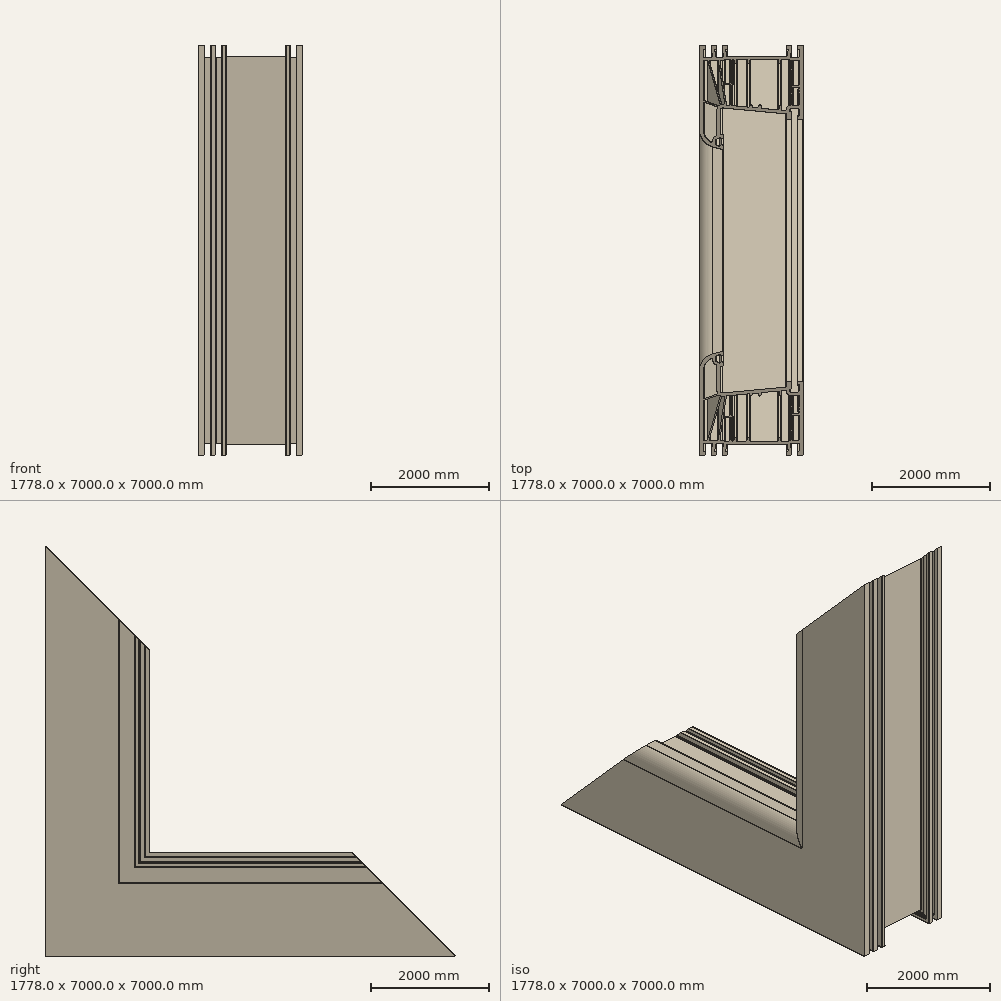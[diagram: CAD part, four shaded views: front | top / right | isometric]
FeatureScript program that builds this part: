
annotation { "Feature Type Name" : "Feature", "Feature Type Description" : "" }
export const myFeature = defineFeature(function(context is Context, id is Id, definition is map)
    precondition{}
    {
        {
            var Q0;
            Q0=qCreatedBy(makeId("Front.planeOp"),FACE);
            var sketch = newSketch(context, id + "F0", { "sketchPlane" : qUnion([Q0])});
            skLineSegment(sketch, "E0", {"start": v(-889, -889) * mm, "end": v(-787.4, -889) * mm});
            skLineSegment(sketch, "E1", {"start": v(-508, 723.9) * mm, "end": v(-520.7, 723.9) * mm});
            skLineSegment(sketch, "E2", {"start": v(-520.7, 723.9) * mm, "end": v(-520.7, 701.04) * mm});
            skLineSegment(sketch, "E3", {"start": v(787.4, -889) * mm, "end": v(889, -889) * mm});
            skLineSegment(sketch, "E4", {"start": v(889, -889) * mm, "end": v(889, 355.6) * mm});
            skLineSegment(sketch, "E5", {"start": v(863.6, 381) * mm, "end": v(787.4, 381) * mm});
            skLineSegment(sketch, "E6", {"start": v(787.4, 381) * mm, "end": v(787.4, 314.96) * mm});
            skLineSegment(sketch, "E7", {"start": v(673.1, 241.3) * mm, "end": v(685.8, 241.3) * mm});
            skLineSegment(sketch, "E8", {"start": v(685.8, 241.3) * mm, "end": v(685.8, 381) * mm});
            skLineSegment(sketch, "E9", {"start": v(685.8, 381) * mm, "end": v(596.9, 381) * mm});
            skLineSegment(sketch, "E10", {"start": v(-889, 548.53) * mm, "end": v(-889, -889) * mm});
            skLineSegment(sketch, "E11", {"start": v(-482.6, 698.5) * mm, "end": v(-508, 723.9) * mm});
            skLineSegment(sketch, "E12", {"start": v(-482.6, 647.7) * mm, "end": v(-482.6, 698.5) * mm});
            skLineSegment(sketch, "E13", {"start": v(-520.7, 635) * mm, "end": v(-495.3, 635) * mm});
            skLineSegment(sketch, "E14", {"start": v(-589.28, 648.94) * mm, "end": v(-589.28, 635) * mm});
            skLineSegment(sketch, "E15", {"start": v(-623.74, 673.1) * mm, "end": v(-596.61, 660.45) * mm});
            skLineSegment(sketch, "E16", {"start": v(-660.4, 753.62) * mm, "end": v(-660.4, 730.65) * mm});
            skLineSegment(sketch, "E17", {"start": v(-820.42, 91.47) * mm, "end": v(-820.42, 548.53) * mm});
            skLineSegment(sketch, "E18", {"start": v(-812.06, 49.34) * mm, "end": v(-561.15, 140.67) * mm});
            skLineSegment(sketch, "E19", {"start": v(-820.42, -617.22) * mm, "end": v(-820.42, 37.41) * mm});
            skLineSegment(sketch, "E20", {"start": v(-587.31, 158.18) * mm, "end": v(-803.38, 79.54) * mm});
            skLineSegment(sketch, "E21", {"start": v(820.42, -215.9) * mm, "end": v(820.42, -617.22) * mm});
            skLineSegment(sketch, "E22", {"start": v(718.82, -203.2) * mm, "end": v(807.72, -203.2) * mm});
            skLineSegment(sketch, "E23", {"start": v(706.12, -617.22) * mm, "end": v(706.12, -215.9) * mm});
            skLineSegment(sketch, "E24", {"start": v(680.72, -495.3) * mm, "end": v(680.72, -618.92) * mm});
            skLineSegment(sketch, "E25", {"start": v(665.48, -482.6) * mm, "end": v(668.02, -482.6) * mm});
            skLineSegment(sketch, "E26", {"start": v(665.48, -457.2) * mm, "end": v(665.48, -482.6) * mm});
            skLineSegment(sketch, "E27", {"start": v(668.02, -457.2) * mm, "end": v(665.48, -457.2) * mm});
            skLineSegment(sketch, "E28", {"start": v(680.72, -88.9) * mm, "end": v(680.72, -444.5) * mm});
            skLineSegment(sketch, "E29", {"start": v(665.48, -76.2) * mm, "end": v(668.02, -76.2) * mm});
            skLineSegment(sketch, "E30", {"start": v(665.48, -50.8) * mm, "end": v(665.48, -76.2) * mm});
            skLineSegment(sketch, "E31", {"start": v(668.02, -50.8) * mm, "end": v(665.48, -50.8) * mm});
            skLineSegment(sketch, "E32", {"start": v(680.72, 122.06) * mm, "end": v(680.72, -38.1) * mm});
            skLineSegment(sketch, "E33", {"start": v(706.12, -165.1) * mm, "end": v(706.12, 121.92) * mm});
            skLineSegment(sketch, "E34", {"start": v(807.72, -177.8) * mm, "end": v(718.82, -177.8) * mm});
            skLineSegment(sketch, "E35", {"start": v(820.42, -152.4) * mm, "end": v(820.42, -165.1) * mm});
            skLineSegment(sketch, "E36", {"start": v(787.4, -139.7) * mm, "end": v(807.72, -139.7) * mm});
            skLineSegment(sketch, "E37", {"start": v(787.4, -114.3) * mm, "end": v(787.4, -139.7) * mm});
            skLineSegment(sketch, "E38", {"start": v(807.72, -114.3) * mm, "end": v(787.4, -114.3) * mm});
            skLineSegment(sketch, "E39", {"start": v(787.4, -88.9) * mm, "end": v(807.72, -88.9) * mm});
            skLineSegment(sketch, "E40", {"start": v(787.4, -63.5) * mm, "end": v(787.4, -88.9) * mm});
            skLineSegment(sketch, "E41", {"start": v(807.72, -63.5) * mm, "end": v(787.4, -63.5) * mm});
            skLineSegment(sketch, "E42", {"start": v(820.42, 121.92) * mm, "end": v(820.42, -50.8) * mm});
            skLineSegment(sketch, "E43", {"start": v(820.42, 314.96) * mm, "end": v(820.42, 215.9) * mm});
            skLineSegment(sketch, "E44", {"start": v(787.4, 314.96) * mm, "end": v(820.42, 314.96) * mm});
            skLineSegment(sketch, "E45", {"start": v(-520.7, 822.96) * mm, "end": v(-520.7, 800.1) * mm});
            skLineSegment(sketch, "E46", {"start": v(-602.27, 804.86) * mm, "end": v(-538.77, 834.47) * mm});
            skLineSegment(sketch, "E47", {"start": v(-609.6, 730.65) * mm, "end": v(-609.6, 793.35) * mm});
            skLineSegment(sketch, "E48", {"start": v(-538.77, 689.53) * mm, "end": v(-602.27, 719.14) * mm});
            skLineSegment(sketch, "E49", {"start": v(787.4, -822.96) * mm, "end": v(787.4, -889) * mm});
            skLineSegment(sketch, "E50", {"start": v(820.42, -822.96) * mm, "end": v(787.4, -822.96) * mm});
            skLineSegment(sketch, "E51", {"start": v(820.42, -711.2) * mm, "end": v(820.42, -822.96) * mm});
            skLineSegment(sketch, "E52", {"start": v(525.87, 217.04) * mm, "end": v(578.17, 221.93) * mm});
            skLineSegment(sketch, "E53", {"start": v(179.16, 184.6) * mm, "end": v(462.37, 211.1) * mm});
            skLineSegment(sketch, "E54", {"start": v(26.4, 170.31) * mm, "end": v(102.96, 177.48) * mm});
            skLineSegment(sketch, "E55", {"start": v(-323.76, 137.56) * mm, "end": v(-49.4, 163.22) * mm});
            skLineSegment(sketch, "E56", {"start": v(-417.58, 128.78) * mm, "end": v(-374.56, 132.8) * mm});
            skLineSegment(sketch, "E57", {"start": v(-486.55, 122.33) * mm, "end": v(-469.67, 123.9) * mm});
            skLineSegment(sketch, "E58", {"start": v(-589.28, 635) * mm, "end": v(-589.28, 215.9) * mm});
            skLineSegment(sketch, "E59", {"start": v(-533.4, 215.9) * mm, "end": v(-533.4, 622.3) * mm});
            skLineSegment(sketch, "E60", {"start": v(572.97, 277.57) * mm, "end": v(-491.75, 177.97) * mm});
            skLineSegment(sketch, "E61", {"start": v(795.02, 190.5) * mm, "end": v(673.1, 190.5) * mm});
            skLineSegment(sketch, "E62", {"start": v(718.82, 134.62) * mm, "end": v(807.72, 134.62) * mm});
            skLineSegment(sketch, "E63", {"start": v(-360.68, -248.92) * mm, "end": v(-360.68, -629.92) * mm});
            skLineSegment(sketch, "E64", {"start": v(-470.96, -236.22) * mm, "end": v(-373.38, -236.22) * mm});
            skLineSegment(sketch, "E65", {"start": v(-538.56, -615.34) * mm, "end": v(-483.52, -247.04) * mm});
            skLineSegment(sketch, "E66", {"start": v(-455.93, 109.39) * mm, "end": v(-564.8, -619.1) * mm});
            skLineSegment(sketch, "E67", {"start": v(-476.68, -201.32) * mm, "end": v(-428.96, 118.01) * mm});
            skLineSegment(sketch, "E68", {"start": v(-373.38, -215.9) * mm, "end": v(-464.12, -215.9) * mm});
            skLineSegment(sketch, "E69", {"start": v(-360.68, 120.16) * mm, "end": v(-360.68, -203.2) * mm});
            skLineSegment(sketch, "E70", {"start": v(-335.28, -203.2) * mm, "end": v(-335.28, 124.91) * mm});
            skLineSegment(sketch, "E71", {"start": v(-284.48, -215.9) * mm, "end": v(-322.58, -215.9) * mm});
            skLineSegment(sketch, "E72", {"start": v(-284.48, -241.3) * mm, "end": v(-284.48, -215.9) * mm});
            skLineSegment(sketch, "E73", {"start": v(-322.58, -241.3) * mm, "end": v(-284.48, -241.3) * mm});
            skLineSegment(sketch, "E74", {"start": v(-335.28, -629.92) * mm, "end": v(-335.28, -254) * mm});
            skLineSegment(sketch, "E75", {"start": v(167.64, 152.4) * mm, "end": v(167.64, 171.96) * mm});
            skLineSegment(sketch, "E76", {"start": v(116.84, 164.83) * mm, "end": v(116.84, 152.4) * mm});
            skLineSegment(sketch, "E77", {"start": v(593.11, 279.46) * mm, "end": v(572.97, 277.57) * mm});
            skLineSegment(sketch, "E78", {"start": v(604.58, 293.2) * mm, "end": v(596.9, 381) * mm});
            skLineSegment(sketch, "E79", {"start": v(-482.6, 825.5) * mm, "end": v(-482.6, 881.38) * mm});
            skLineSegment(sketch, "E80", {"start": v(-508, 800.1) * mm, "end": v(-482.6, 825.5) * mm});
            skLineSegment(sketch, "E81", {"start": v(-520.7, 800.1) * mm, "end": v(-508, 800.1) * mm});
            skLineSegment(sketch, "E82", {"start": v(-406.4, -876.3) * mm, "end": v(-406.4, -822.96) * mm});
            skLineSegment(sketch, "E83", {"start": v(-406.4, -822.96) * mm, "end": v(-444.5, -822.96) * mm});
            skLineSegment(sketch, "E84", {"start": v(-444.5, -822.96) * mm, "end": v(-444.5, -793.3) * mm});
            skLineSegment(sketch, "E85", {"start": v(-419.1, -749.3) * mm, "end": v(-419.1, -711.2) * mm});
            skLineSegment(sketch, "E86", {"start": v(-495.3, -876.3) * mm, "end": v(-482.6, -889) * mm});
            skLineSegment(sketch, "E87", {"start": v(-660.4, -749.3) * mm, "end": v(-685.8, -749.3) * mm});
            skLineSegment(sketch, "E88", {"start": v(-685.8, -749.3) * mm, "end": v(-685.8, -876.3) * mm});
            skLineSegment(sketch, "E89", {"start": v(-685.8, -876.3) * mm, "end": v(-673.1, -889) * mm});
            skLineSegment(sketch, "E90", {"start": v(-673.1, -889) * mm, "end": v(-596.9, -889) * mm});
            skLineSegment(sketch, "E91", {"start": v(-596.9, -889) * mm, "end": v(-596.9, -822.96) * mm});
            skLineSegment(sketch, "E92", {"start": v(-596.9, -822.96) * mm, "end": v(-635, -822.96) * mm});
            skLineSegment(sketch, "E93", {"start": v(-635, -822.96) * mm, "end": v(-635, -793.3) * mm});
            skLineSegment(sketch, "E94", {"start": v(-609.6, -749.3) * mm, "end": v(-609.6, -711.2) * mm});
            skLineSegment(sketch, "E95", {"start": v(-660.4, -711.2) * mm, "end": v(-660.4, -749.3) * mm});
            skLineSegment(sketch, "E96", {"start": v(596.9, -822.96) * mm, "end": v(596.9, -876.3) * mm});
            skLineSegment(sketch, "E97", {"start": v(635, -822.96) * mm, "end": v(596.9, -822.96) * mm});
            skLineSegment(sketch, "E98", {"start": v(635, -793.3) * mm, "end": v(635, -822.96) * mm});
            skLineSegment(sketch, "E99", {"start": v(609.6, -711.2) * mm, "end": v(609.6, -749.3) * mm});
            skLineSegment(sketch, "E100", {"start": v(-257.8, -629.92) * mm, "end": v(-257.8, -603.25) * mm});
            skLineSegment(sketch, "E101", {"start": v(-295.9, -603.25) * mm, "end": v(-295.9, -629.92) * mm});
            skLineSegment(sketch, "E102", {"start": v(-31.75, -629.92) * mm, "end": v(-31.75, -603.25) * mm});
            skLineSegment(sketch, "E103", {"start": v(-69.85, -603.25) * mm, "end": v(-69.85, -629.92) * mm});
            skLineSegment(sketch, "E104", {"start": v(499.11, -629.92) * mm, "end": v(499.11, -603.25) * mm});
            skLineSegment(sketch, "E105", {"start": v(461.01, -603.25) * mm, "end": v(461.01, -629.92) * mm});
            skLineSegment(sketch, "E106", {"start": v(-495.3, -749.3) * mm, "end": v(-495.3, -876.3) * mm});
            skLineSegment(sketch, "E107", {"start": v(-469.9, -749.3) * mm, "end": v(-495.3, -749.3) * mm});
            skLineSegment(sketch, "E108", {"start": v(-469.9, -711.2) * mm, "end": v(-469.9, -749.3) * mm});
            skLineSegment(sketch, "E109", {"start": v(-482.6, -889) * mm, "end": v(-419.1, -889) * mm});
            skLineSegment(sketch, "E110", {"start": v(-419.1, -889) * mm, "end": v(-406.4, -876.3) * mm});
            skLineSegment(sketch, "E111", {"start": v(-820.42, -822.96) * mm, "end": v(-820.42, -711.2) * mm});
            skLineSegment(sketch, "E112", {"start": v(-787.4, -822.96) * mm, "end": v(-820.42, -822.96) * mm});
            skLineSegment(sketch, "E113", {"start": v(-787.4, -889) * mm, "end": v(-787.4, -822.96) * mm});
            skLineSegment(sketch, "E114", {"start": v(-492.2, 888.74) * mm, "end": v(-663.09, 842.95) * mm});
            skLineSegment(sketch, "E115", {"start": v(476.25, 198.46) * mm, "end": v(476.25, 146.05) * mm});
            skLineSegment(sketch, "E116", {"start": v(514.35, 146.05) * mm, "end": v(514.35, 204.4) * mm});
            skLineSegment(sketch, "E117", {"start": v(-718.23, -613.72) * mm, "end": v(-509.92, 112.75) * mm});
            skLineSegment(sketch, "E118", {"start": v(-534.56, 118.96) * mm, "end": v(-746.66, -620.72) * mm});
            skLineSegment(sketch, "E119", {"start": v(660.4, -749.3) * mm, "end": v(660.4, -711.2) * mm});
            skLineSegment(sketch, "E120", {"start": v(685.8, -749.3) * mm, "end": v(660.4, -749.3) * mm});
            skLineSegment(sketch, "E121", {"start": v(685.8, -876.3) * mm, "end": v(685.8, -749.3) * mm});
            skLineSegment(sketch, "E122", {"start": v(673.1, -889) * mm, "end": v(685.8, -876.3) * mm});
            skLineSegment(sketch, "E123", {"start": v(609.6, -889) * mm, "end": v(673.1, -889) * mm});
            skLineSegment(sketch, "E124", {"start": v(596.9, -876.3) * mm, "end": v(609.6, -889) * mm});
            skLineSegment(sketch, "E125", {"start": v(-758.87, -629.92) * mm, "end": v(-807.72, -629.92) * mm});
            skLineSegment(sketch, "E126", {"start": v(-577.36, -629.92) * mm, "end": v(-706.02, -629.92) * mm});
            skLineSegment(sketch, "E127", {"start": v(-495.3, -629.92) * mm, "end": v(-526, -629.92) * mm});
            skLineSegment(sketch, "E128", {"start": v(-373.38, -642.62) * mm, "end": v(-448.12, -642.62) * mm});
            skLineSegment(sketch, "E129", {"start": v(-308.6, -642.62) * mm, "end": v(-322.58, -642.62) * mm});
            skLineSegment(sketch, "E130", {"start": v(-82.55, -642.62) * mm, "end": v(-245.1, -642.62) * mm});
            skLineSegment(sketch, "E131", {"start": v(448.31, -642.62) * mm, "end": v(-19.05, -642.62) * mm});
            skLineSegment(sketch, "E132", {"start": v(638.62, -642.62) * mm, "end": v(511.81, -642.62) * mm});
            skLineSegment(sketch, "E133", {"start": v(807.72, -629.92) * mm, "end": v(718.82, -629.92) * mm});
            skLineSegment(sketch, "E134", {"start": v(685.8, -685.8) * mm, "end": v(795.02, -685.8) * mm});
            skLineSegment(sketch, "E135", {"start": v(-406.4, -698.5) * mm, "end": v(596.9, -698.5) * mm});
            skLineSegment(sketch, "E136", {"start": v(-584.2, -685.8) * mm, "end": v(-495.3, -685.8) * mm});
            skLineSegment(sketch, "E137", {"start": v(-795.02, -685.8) * mm, "end": v(-685.8, -685.8) * mm});
            skArc(sketch, "E138", {"start": v(-663.09, 842.95) * mm, "mid": v(-826.01, 734.09) * mm, "end": v(-889, 548.53) * mm});
            skArc(sketch, "E139", {"start": v(604.58, 293.2) * mm, "mid": v(601.68, 283.97) * mm, "end": v(593.11, 279.46) * mm});
            skArc(sketch, "E140", {"start": v(647.76, 214.11) * mm, "mid": v(654.52, 233.22) * mm, "end": v(673.1, 241.3) * mm});
            skArc(sketch, "E141", {"start": v(514.35, 204.4) * mm, "mid": v(517.66, 212.95) * mm, "end": v(525.87, 217.04) * mm});
            skArc(sketch, "E142", {"start": v(462.37, 211.1) * mm, "mid": v(472.1, 207.84) * mm, "end": v(476.25, 198.46) * mm});
            skArc(sketch, "E143", {"start": v(476.25, 146.05) * mm, "mid": v(495.3, 127) * mm, "end": v(514.35, 146.05) * mm});
            skArc(sketch, "E144", {"start": v(-49.4, 163.22) * mm, "mid": v(-39.9, 160.17) * mm, "end": v(-35.53, 151.19) * mm});
            skArc(sketch, "E145", {"start": v(15, 155.91) * mm, "mid": v(17.61, 165.55) * mm, "end": v(26.4, 170.31) * mm});
            skArc(sketch, "E146", {"start": v(-35.53, 151.19) * mm, "mid": v(-7.8, 127.11) * mm, "end": v(15, 155.91) * mm});
            skArc(sketch, "E147", {"start": v(-706.02, -629.92) * mm, "mid": v(-716.17, -624.86) * mm, "end": v(-718.23, -613.72) * mm});
            skArc(sketch, "E148", {"start": v(-509.92, 112.75) * mm, "mid": v(-505.24, 119.48) * mm, "end": v(-497.42, 121.94) * mm});
            skArc(sketch, "E149", {"start": v(-540.64, 133.58) * mm, "mid": v(-535.04, 127.33) * mm, "end": v(-534.56, 118.96) * mm});
            skArc(sketch, "E150", {"start": v(-746.66, -620.72) * mm, "mid": v(-751.23, -627.36) * mm, "end": v(-758.87, -629.92) * mm});
            skArc(sketch, "E151", {"start": v(660.4, -711.2) * mm, "mid": v(661.27, -704.63) * mm, "end": v(663.8, -698.5) * mm});
            skArc(sketch, "E152", {"start": v(609.6, -749.3) * mm, "mid": v(616.4, -774.7) * mm, "end": v(635, -793.3) * mm});
            skArc(sketch, "E153", {"start": v(596.9, -698.5) * mm, "mid": v(605.88, -702.22) * mm, "end": v(609.6, -711.2) * mm});
            skArc(sketch, "E154", {"start": v(-807.72, -629.92) * mm, "mid": v(-816.7, -626.2) * mm, "end": v(-820.42, -617.22) * mm});
            skArc(sketch, "E155", {"start": v(-454.5, -640.9) * mm, "mid": v(-474.17, -632.71) * mm, "end": v(-495.3, -629.92) * mm});
            skArc(sketch, "E156", {"start": v(-448.12, -642.62) * mm, "mid": v(-451.42, -642.18) * mm, "end": v(-454.5, -640.9) * mm});
            skArc(sketch, "E157", {"start": v(645, -640.9) * mm, "mid": v(641.92, -642.18) * mm, "end": v(638.62, -642.62) * mm});
            skArc(sketch, "E158", {"start": v(670.42, -631.39) * mm, "mid": v(657.3, -635.08) * mm, "end": v(645, -640.9) * mm});
            skArc(sketch, "E159", {"start": v(820.42, -617.22) * mm, "mid": v(816.7, -626.2) * mm, "end": v(807.72, -629.92) * mm});
            skArc(sketch, "E160", {"start": v(795.02, -685.8) * mm, "mid": v(812.98, -693.24) * mm, "end": v(820.42, -711.2) * mm});
            skArc(sketch, "E161", {"start": v(-495.3, -685.8) * mm, "mid": v(-482.6, -689.2) * mm, "end": v(-473.3, -698.5) * mm});
            skArc(sketch, "E162", {"start": v(-820.42, -711.2) * mm, "mid": v(-812.98, -693.24) * mm, "end": v(-795.02, -685.8) * mm});
            skArc(sketch, "E163", {"start": v(663.8, -698.5) * mm, "mid": v(673.1, -689.2) * mm, "end": v(685.8, -685.8) * mm});
            skArc(sketch, "E164", {"start": v(-69.85, -629.92) * mm, "mid": v(-73.57, -638.9) * mm, "end": v(-82.55, -642.62) * mm});
            skArc(sketch, "E165", {"start": v(-31.75, -603.25) * mm, "mid": v(-50.8, -584.2) * mm, "end": v(-69.85, -603.25) * mm});
            skArc(sketch, "E166", {"start": v(-19.05, -642.62) * mm, "mid": v(-28.03, -638.9) * mm, "end": v(-31.75, -629.92) * mm});
            skArc(sketch, "E167", {"start": v(-245.1, -642.62) * mm, "mid": v(-254.1, -638.9) * mm, "end": v(-257.8, -629.92) * mm});
            skArc(sketch, "E168", {"start": v(-257.8, -603.25) * mm, "mid": v(-276.86, -584.2) * mm, "end": v(-295.9, -603.25) * mm});
            skArc(sketch, "E169", {"start": v(-295.9, -629.92) * mm, "mid": v(-299.63, -638.9) * mm, "end": v(-308.6, -642.62) * mm});
            skArc(sketch, "E170", {"start": v(511.81, -642.62) * mm, "mid": v(502.83, -638.9) * mm, "end": v(499.11, -629.92) * mm});
            skArc(sketch, "E171", {"start": v(499.11, -603.25) * mm, "mid": v(480.06, -584.2) * mm, "end": v(461.01, -603.25) * mm});
            skArc(sketch, "E172", {"start": v(461.01, -629.92) * mm, "mid": v(457.3, -638.9) * mm, "end": v(448.31, -642.62) * mm});
            skArc(sketch, "E173", {"start": v(-473.3, -698.5) * mm, "mid": v(-470.77, -704.63) * mm, "end": v(-469.9, -711.2) * mm});
            skArc(sketch, "E174", {"start": v(-444.5, -793.3) * mm, "mid": v(-425.9, -774.7) * mm, "end": v(-419.1, -749.3) * mm});
            skArc(sketch, "E175", {"start": v(-419.1, -711.2) * mm, "mid": v(-415.38, -702.22) * mm, "end": v(-406.4, -698.5) * mm});
            skArc(sketch, "E176", {"start": v(-685.8, -685.8) * mm, "mid": v(-667.84, -693.24) * mm, "end": v(-660.4, -711.2) * mm});
            skArc(sketch, "E177", {"start": v(-635, -793.3) * mm, "mid": v(-616.4, -774.7) * mm, "end": v(-609.6, -749.3) * mm});
            skArc(sketch, "E178", {"start": v(-609.6, -711.2) * mm, "mid": v(-602.16, -693.24) * mm, "end": v(-584.2, -685.8) * mm});
            skArc(sketch, "E179", {"start": v(-482.6, 881.38) * mm, "mid": v(-485.58, 887.43) * mm, "end": v(-492.2, 888.74) * mm});
            skArc(sketch, "E180", {"start": v(-538.77, 834.47) * mm, "mid": v(-526.58, 833.67) * mm, "end": v(-520.7, 822.96) * mm});
            skArc(sketch, "E181", {"start": v(-609.6, 793.35) * mm, "mid": v(-607.61, 800.17) * mm, "end": v(-602.27, 804.86) * mm});
            skArc(sketch, "E182", {"start": v(-602.27, 719.14) * mm, "mid": v(-607.61, 723.83) * mm, "end": v(-609.6, 730.65) * mm});
            skArc(sketch, "E183", {"start": v(-520.7, 701.04) * mm, "mid": v(-526.58, 690.33) * mm, "end": v(-538.77, 689.53) * mm});
            skArc(sketch, "E184", {"start": v(-495.3, 635) * mm, "mid": v(-486.32, 638.72) * mm, "end": v(-482.6, 647.7) * mm});
            skArc(sketch, "E185", {"start": v(-596.61, 660.45) * mm, "mid": v(-591.27, 655.77) * mm, "end": v(-589.28, 648.94) * mm});
            skArc(sketch, "E186", {"start": v(-660.4, 730.65) * mm, "mid": v(-650.46, 696.53) * mm, "end": v(-623.74, 673.1) * mm});
            skArc(sketch, "E187", {"start": v(-678.15, 765.27) * mm, "mid": v(-666.13, 764.23) * mm, "end": v(-660.4, 753.62) * mm});
            skArc(sketch, "E188", {"start": v(-820.42, 548.53) * mm, "mid": v(-781.68, 678.16) * mm, "end": v(-678.15, 765.27) * mm});
            skArc(sketch, "E189", {"start": v(-561.15, 140.67) * mm, "mid": v(-555.13, 141.32) * mm, "end": v(-549.48, 139.11) * mm});
            skArc(sketch, "E190", {"start": v(-820.42, 37.41) * mm, "mid": v(-818.12, 44.7) * mm, "end": v(-812.06, 49.34) * mm});
            skArc(sketch, "E191", {"start": v(-803.38, 79.54) * mm, "mid": v(-815, 81.07) * mm, "end": v(-820.42, 91.47) * mm});
            skArc(sketch, "E192", {"start": v(-580.18, 175.56) * mm, "mid": v(-579.9, 165.3) * mm, "end": v(-587.31, 158.18) * mm});
            skArc(sketch, "E193", {"start": v(807.72, -203.2) * mm, "mid": v(816.7, -206.92) * mm, "end": v(820.42, -215.9) * mm});
            skArc(sketch, "E194", {"start": v(706.12, -215.9) * mm, "mid": v(709.84, -206.92) * mm, "end": v(718.82, -203.2) * mm});
            skArc(sketch, "E195", {"start": v(718.82, -629.92) * mm, "mid": v(709.84, -626.2) * mm, "end": v(706.12, -617.22) * mm});
            skArc(sketch, "E196", {"start": v(680.72, -618.92) * mm, "mid": v(677.81, -627) * mm, "end": v(670.42, -631.39) * mm});
            skArc(sketch, "E197", {"start": v(668.02, -482.6) * mm, "mid": v(677, -486.32) * mm, "end": v(680.72, -495.3) * mm});
            skArc(sketch, "E198", {"start": v(680.72, -444.5) * mm, "mid": v(677, -453.48) * mm, "end": v(668.02, -457.2) * mm});
            skArc(sketch, "E199", {"start": v(668.02, -76.2) * mm, "mid": v(677, -79.92) * mm, "end": v(680.72, -88.9) * mm});
            skArc(sketch, "E200", {"start": v(680.72, -38.1) * mm, "mid": v(677, -47.08) * mm, "end": v(668.02, -50.8) * mm});
            skArc(sketch, "E201", {"start": v(668.7, 134.74) * mm, "mid": v(677.24, 130.8) * mm, "end": v(680.72, 122.06) * mm});
            skArc(sketch, "E202", {"start": v(706.12, 121.92) * mm, "mid": v(709.84, 130.9) * mm, "end": v(718.82, 134.62) * mm});
            skArc(sketch, "E203", {"start": v(718.82, -177.8) * mm, "mid": v(709.84, -174.08) * mm, "end": v(706.12, -165.1) * mm});
            skArc(sketch, "E204", {"start": v(820.42, -165.1) * mm, "mid": v(816.7, -174.08) * mm, "end": v(807.72, -177.8) * mm});
            skArc(sketch, "E205", {"start": v(807.72, -139.7) * mm, "mid": v(816.7, -143.42) * mm, "end": v(820.42, -152.4) * mm});
            skArc(sketch, "E206", {"start": v(820.42, -101.6) * mm, "mid": v(816.7, -110.58) * mm, "end": v(807.72, -114.3) * mm});
            skArc(sketch, "E207", {"start": v(807.72, -88.9) * mm, "mid": v(816.7, -92.62) * mm, "end": v(820.42, -101.6) * mm});
            skArc(sketch, "E208", {"start": v(820.42, -50.8) * mm, "mid": v(816.7, -59.78) * mm, "end": v(807.72, -63.5) * mm});
            skArc(sketch, "E209", {"start": v(889, 355.6) * mm, "mid": v(881.56, 373.56) * mm, "end": v(863.6, 381) * mm});
            skArc(sketch, "E210", {"start": v(807.72, 134.62) * mm, "mid": v(816.7, 130.9) * mm, "end": v(820.42, 121.92) * mm});
            skArc(sketch, "E211", {"start": v(578.17, 221.93) * mm, "mid": v(587.57, 218.97) * mm, "end": v(592.02, 210.18) * mm});
            skArc(sketch, "E212", {"start": v(-497.42, 121.94) * mm, "mid": v(-491.98, 121.98) * mm, "end": v(-486.55, 122.33) * mm});
            skArc(sketch, "E213", {"start": v(-549.48, 139.11) * mm, "mid": v(-545.14, 136.22) * mm, "end": v(-540.64, 133.58) * mm});
            skArc(sketch, "E214", {"start": v(-589.28, 215.9) * mm, "mid": v(-586.98, 195.23) * mm, "end": v(-580.18, 175.56) * mm});
            skArc(sketch, "E215", {"start": v(-533.4, 622.3) * mm, "mid": v(-529.68, 631.28) * mm, "end": v(-520.7, 635) * mm});
            skArc(sketch, "E216", {"start": v(-491.75, 177.97) * mm, "mid": v(-520.96, 187.73) * mm, "end": v(-533.4, 215.9) * mm});
            skArc(sketch, "E217", {"start": v(673.1, 190.5) * mm, "mid": v(655.78, 197.32) * mm, "end": v(647.76, 214.11) * mm});
            skArc(sketch, "E218", {"start": v(820.42, 215.9) * mm, "mid": v(812.98, 197.94) * mm, "end": v(795.02, 190.5) * mm});
            skArc(sketch, "E219", {"start": v(592.02, 210.18) * mm, "mid": v(616.1, 157.96) * mm, "end": v(668.7, 134.74) * mm});
            skArc(sketch, "E220", {"start": v(-360.68, -629.92) * mm, "mid": v(-364.4, -638.9) * mm, "end": v(-373.38, -642.62) * mm});
            skArc(sketch, "E221", {"start": v(-373.38, -236.22) * mm, "mid": v(-364.4, -239.94) * mm, "end": v(-360.68, -248.92) * mm});
            skArc(sketch, "E222", {"start": v(-483.52, -247.04) * mm, "mid": v(-479.25, -239.3) * mm, "end": v(-470.96, -236.22) * mm});
            skArc(sketch, "E223", {"start": v(-526, -629.92) * mm, "mid": v(-535.62, -625.51) * mm, "end": v(-538.56, -615.34) * mm});
            skArc(sketch, "E224", {"start": v(-564.8, -619.1) * mm, "mid": v(-569.07, -626.84) * mm, "end": v(-577.36, -629.92) * mm});
            skArc(sketch, "E225", {"start": v(-469.67, 123.9) * mm, "mid": v(-459.27, 120) * mm, "end": v(-455.93, 109.39) * mm});
            skArc(sketch, "E226", {"start": v(-428.96, 118.01) * mm, "mid": v(-425.13, 125.36) * mm, "end": v(-417.58, 128.78) * mm});
            skArc(sketch, "E227", {"start": v(-464.12, -215.9) * mm, "mid": v(-473.74, -211.5) * mm, "end": v(-476.68, -201.32) * mm});
            skArc(sketch, "E228", {"start": v(-360.68, -203.2) * mm, "mid": v(-364.4, -212.18) * mm, "end": v(-373.38, -215.9) * mm});
            skArc(sketch, "E229", {"start": v(-374.56, 132.8) * mm, "mid": v(-364.83, 129.55) * mm, "end": v(-360.68, 120.16) * mm});
            skArc(sketch, "E230", {"start": v(-335.28, 124.91) * mm, "mid": v(-331.97, 133.46) * mm, "end": v(-323.76, 137.56) * mm});
            skArc(sketch, "E231", {"start": v(-322.58, -215.9) * mm, "mid": v(-331.56, -212.18) * mm, "end": v(-335.28, -203.2) * mm});
            skArc(sketch, "E232", {"start": v(-322.58, -642.62) * mm, "mid": v(-331.56, -638.9) * mm, "end": v(-335.28, -629.92) * mm});
            skArc(sketch, "E233", {"start": v(-335.28, -254) * mm, "mid": v(-331.56, -245.02) * mm, "end": v(-322.58, -241.3) * mm});
            skArc(sketch, "E234", {"start": v(167.64, 171.96) * mm, "mid": v(170.95, 180.51) * mm, "end": v(179.16, 184.6) * mm});
            skArc(sketch, "E235", {"start": v(102.96, 177.48) * mm, "mid": v(112.7, 174.22) * mm, "end": v(116.84, 164.83) * mm});
            skArc(sketch, "E236", {"start": v(116.84, 152.4) * mm, "mid": v(142.24, 127) * mm, "end": v(167.64, 152.4) * mm});
            skSolve(sketch);
        }
        {
            var Q0;
            Q0=makeQuery(id+"F0.imprint","IMPRINT",FACE,{"disambiguationData":[TD([[makeQuery(id+"F0.imprint","IMPRINT",EDGE,{"derivedFrom":sQuery(id+"F0.wireOp",EDGE,"E0")}),1.0]])]});
            extrude(context, id + "F1", {"entities" : qUnion([Q0]), "depth" : 7000 * mm, "offsetDistance" : 25 * mm});
        }
        {
            var Q0;
            Q0=makeQuery(id+"F1.opExtrude","SWEPT_FACE",FACE,{"disambiguationData":[OSD([sQuery(id+"F0.wireOp",EDGE,"E10")])]});
            var sketch = newSketch(context, id + "F2", { "sketchPlane" : qUnion([Q0])});
            skLineSegment(sketch, "E237", {"start": v(7000, -889) * mm, "end": v(7000, 987.98) * mm});
            skLineSegment(sketch, "E238", {"start": v(7000, 987.98) * mm, "end": v(5123.02, 987.98) * mm});
            skLineSegment(sketch, "E239", {"start": v(5123.02, 987.98) * mm, "end": v(7000, -889) * mm});
            skSolve(sketch);
        }
        {
            var Q0;
            {var subQ0=sQuery(id+"F2.wireOp",EDGE,"E239");var subQ1=sQuery(id+"F2.wireOp",EDGE,"E237");var subQ2=sQuery(id+"F0.wireOp",EDGE,"E10");var subQ3=makeQuery(id+"F2.imprint","INTERSECT",VERTEX,{"derivedFrom":[makeQuery(id+"F1.opExtrude","SWEPT_EDGE",EDGE,{"disambiguationData":[OSD([sQuery(id+"F0.wireOp",EDGE,"E0"),subQ2])]}),subQ1,subQ0]});Q0=makeQuery(id+"F2.imprint","IMPRINT",FACE,{"disambiguationData":[TD([[makeQuery(id+"F2.imprint","IMPRINT",EDGE,{"disambiguationData":[TD([[subQ3,1.0]])],"derivedFrom":subQ1}),-1.0]])]});}
            var Q1;
            {var subQ3=sQuery(id+"F2.wireOp",EDGE,"E238");Q1=makeQuery(id+"F2.imprint","IMPRINT",FACE,{"disambiguationData":[TD([[makeQuery(id+"F2.imprint","IMPRINT",EDGE,{"derivedFrom":subQ3}),1.0]])]});}
            extrude(context, id + "F3", {"entities" : qUnion([Q0, Q1]), "operationType" : NewBodyOperationType.REMOVE, "endBound" : BoundingType.THROUGH_ALL, "oppositeDirection" : true, "depth" : 25 * mm, "offsetDistance" : 25 * mm});
        }
        {
            var Q0;
            Q0=makeQuery(id+"F1.opExtrude","SWEPT_BODY",BODY,{"disambiguationData":[OSD([sQuery(id+"F0.wireOp",EDGE,"E0"),sQuery(id+"F0.wireOp",EDGE,"E10"),sQuery(id+"F0.wireOp",EDGE,"E79"),sQuery(id+"F0.wireOp",EDGE,"E80"),sQuery(id+"F0.wireOp",EDGE,"E81"),sQuery(id+"F0.wireOp",EDGE,"E45"),sQuery(id+"F0.wireOp",EDGE,"E46"),sQuery(id+"F0.wireOp",EDGE,"E47"),sQuery(id+"F0.wireOp",EDGE,"E48"),sQuery(id+"F0.wireOp",EDGE,"E2"),sQuery(id+"F0.wireOp",EDGE,"E1"),sQuery(id+"F0.wireOp",EDGE,"E11"),sQuery(id+"F0.wireOp",EDGE,"E12"),sQuery(id+"F0.wireOp",EDGE,"E13"),sQuery(id+"F0.wireOp",EDGE,"E14"),sQuery(id+"F0.wireOp",EDGE,"E15"),sQuery(id+"F0.wireOp",EDGE,"E16"),sQuery(id+"F0.wireOp",EDGE,"E17"),sQuery(id+"F0.wireOp",EDGE,"E20"),sQuery(id+"F0.wireOp",EDGE,"E18"),sQuery(id+"F0.wireOp",EDGE,"E19"),sQuery(id+"F0.wireOp",EDGE,"E21"),sQuery(id+"F0.wireOp",EDGE,"E22"),sQuery(id+"F0.wireOp",EDGE,"E23"),sQuery(id+"F0.wireOp",EDGE,"E24"),sQuery(id+"F0.wireOp",EDGE,"E25"),sQuery(id+"F0.wireOp",EDGE,"E26"),sQuery(id+"F0.wireOp",EDGE,"E27"),sQuery(id+"F0.wireOp",EDGE,"E28"),sQuery(id+"F0.wireOp",EDGE,"E29"),sQuery(id+"F0.wireOp",EDGE,"E30"),sQuery(id+"F0.wireOp",EDGE,"E31"),sQuery(id+"F0.wireOp",EDGE,"E32"),sQuery(id+"F0.wireOp",EDGE,"E33"),sQuery(id+"F0.wireOp",EDGE,"E34"),sQuery(id+"F0.wireOp",EDGE,"E35"),sQuery(id+"F0.wireOp",EDGE,"E36"),sQuery(id+"F0.wireOp",EDGE,"E37"),sQuery(id+"F0.wireOp",EDGE,"E38"),sQuery(id+"F0.wireOp",EDGE,"E39"),sQuery(id+"F0.wireOp",EDGE,"E40"),sQuery(id+"F0.wireOp",EDGE,"E41"),sQuery(id+"F0.wireOp",EDGE,"E42"),sQuery(id+"F0.wireOp",EDGE,"E43"),sQuery(id+"F0.wireOp",EDGE,"E44"),sQuery(id+"F0.wireOp",EDGE,"E6"),sQuery(id+"F0.wireOp",EDGE,"E5"),sQuery(id+"F0.wireOp",EDGE,"E4"),sQuery(id+"F0.wireOp",EDGE,"E3"),sQuery(id+"F0.wireOp",EDGE,"E49"),sQuery(id+"F0.wireOp",EDGE,"E50"),sQuery(id+"F0.wireOp",EDGE,"E51"),sQuery(id+"F0.wireOp",EDGE,"E52"),sQuery(id+"F0.wireOp",EDGE,"E53"),sQuery(id+"F0.wireOp",EDGE,"E54"),sQuery(id+"F0.wireOp",EDGE,"E55"),sQuery(id+"F0.wireOp",EDGE,"E56"),sQuery(id+"F0.wireOp",EDGE,"E57"),sQuery(id+"F0.wireOp",EDGE,"E58"),sQuery(id+"F0.wireOp",EDGE,"E59"),sQuery(id+"F0.wireOp",EDGE,"E60"),sQuery(id+"F0.wireOp",EDGE,"E61"),sQuery(id+"F0.wireOp",EDGE,"E62"),sQuery(id+"F0.wireOp",EDGE,"E75"),sQuery(id+"F0.wireOp",EDGE,"E76"),sQuery(id+"F0.wireOp",EDGE,"E63"),sQuery(id+"F0.wireOp",EDGE,"E64"),sQuery(id+"F0.wireOp",EDGE,"E65"),sQuery(id+"F0.wireOp",EDGE,"E66"),sQuery(id+"F0.wireOp",EDGE,"E67"),sQuery(id+"F0.wireOp",EDGE,"E68"),sQuery(id+"F0.wireOp",EDGE,"E69"),sQuery(id+"F0.wireOp",EDGE,"E70"),sQuery(id+"F0.wireOp",EDGE,"E71"),sQuery(id+"F0.wireOp",EDGE,"E72"),sQuery(id+"F0.wireOp",EDGE,"E73"),sQuery(id+"F0.wireOp",EDGE,"E74"),sQuery(id+"F0.wireOp",EDGE,"E77"),sQuery(id+"F0.wireOp",EDGE,"E78"),sQuery(id+"F0.wireOp",EDGE,"E9"),sQuery(id+"F0.wireOp",EDGE,"E8"),sQuery(id+"F0.wireOp",EDGE,"E7"),sQuery(id+"F0.wireOp",EDGE,"E96"),sQuery(id+"F0.wireOp",EDGE,"E97"),sQuery(id+"F0.wireOp",EDGE,"E98"),sQuery(id+"F0.wireOp",EDGE,"E99"),sQuery(id+"F0.wireOp",EDGE,"E103"),sQuery(id+"F0.wireOp",EDGE,"E102"),sQuery(id+"F0.wireOp",EDGE,"E100"),sQuery(id+"F0.wireOp",EDGE,"E101"),sQuery(id+"F0.wireOp",EDGE,"E104"),sQuery(id+"F0.wireOp",EDGE,"E105"),sQuery(id+"F0.wireOp",EDGE,"E106"),sQuery(id+"F0.wireOp",EDGE,"E107"),sQuery(id+"F0.wireOp",EDGE,"E108"),sQuery(id+"F0.wireOp",EDGE,"E109"),sQuery(id+"F0.wireOp",EDGE,"E110"),sQuery(id+"F0.wireOp",EDGE,"E83"),sQuery(id+"F0.wireOp",EDGE,"E84"),sQuery(id+"F0.wireOp",EDGE,"E85"),sQuery(id+"F0.wireOp",EDGE,"E86"),sQuery(id+"F0.wireOp",EDGE,"E82"),sQuery(id+"F0.wireOp",EDGE,"E87"),sQuery(id+"F0.wireOp",EDGE,"E91"),sQuery(id+"F0.wireOp",EDGE,"E92"),sQuery(id+"F0.wireOp",EDGE,"E93"),sQuery(id+"F0.wireOp",EDGE,"E94"),sQuery(id+"F0.wireOp",EDGE,"E88"),sQuery(id+"F0.wireOp",EDGE,"E95"),sQuery(id+"F0.wireOp",EDGE,"E90"),sQuery(id+"F0.wireOp",EDGE,"E89"),sQuery(id+"F0.wireOp",EDGE,"E116"),sQuery(id+"F0.wireOp",EDGE,"E115"),sQuery(id+"F0.wireOp",EDGE,"E117"),sQuery(id+"F0.wireOp",EDGE,"E118"),sQuery(id+"F0.wireOp",EDGE,"E125"),sQuery(id+"F0.wireOp",EDGE,"E126"),sQuery(id+"F0.wireOp",EDGE,"E127"),sQuery(id+"F0.wireOp",EDGE,"E128"),sQuery(id+"F0.wireOp",EDGE,"E129"),sQuery(id+"F0.wireOp",EDGE,"E130"),sQuery(id+"F0.wireOp",EDGE,"E131"),sQuery(id+"F0.wireOp",EDGE,"E132"),sQuery(id+"F0.wireOp",EDGE,"E133"),sQuery(id+"F0.wireOp",EDGE,"E134"),sQuery(id+"F0.wireOp",EDGE,"E135"),sQuery(id+"F0.wireOp",EDGE,"E136"),sQuery(id+"F0.wireOp",EDGE,"E137"),sQuery(id+"F0.wireOp",EDGE,"E119"),sQuery(id+"F0.wireOp",EDGE,"E120"),sQuery(id+"F0.wireOp",EDGE,"E121"),sQuery(id+"F0.wireOp",EDGE,"E122"),sQuery(id+"F0.wireOp",EDGE,"E123"),sQuery(id+"F0.wireOp",EDGE,"E124"),sQuery(id+"F0.wireOp",EDGE,"E114"),sQuery(id+"F0.wireOp",EDGE,"E111"),sQuery(id+"F0.wireOp",EDGE,"E112"),sQuery(id+"F0.wireOp",EDGE,"E113"),sQuery(id+"F0.wireOp",EDGE,"E139"),sQuery(id+"F0.wireOp",EDGE,"E140"),sQuery(id+"F0.wireOp",EDGE,"E141"),sQuery(id+"F0.wireOp",EDGE,"E142"),sQuery(id+"F0.wireOp",EDGE,"E143"),sQuery(id+"F0.wireOp",EDGE,"E144"),sQuery(id+"F0.wireOp",EDGE,"E145"),sQuery(id+"F0.wireOp",EDGE,"E146"),sQuery(id+"F0.wireOp",EDGE,"E147"),sQuery(id+"F0.wireOp",EDGE,"E148"),sQuery(id+"F0.wireOp",EDGE,"E149"),sQuery(id+"F0.wireOp",EDGE,"E150"),sQuery(id+"F0.wireOp",EDGE,"E154"),sQuery(id+"F0.wireOp",EDGE,"E155"),sQuery(id+"F0.wireOp",EDGE,"E156"),sQuery(id+"F0.wireOp",EDGE,"E157"),sQuery(id+"F0.wireOp",EDGE,"E158"),sQuery(id+"F0.wireOp",EDGE,"E159"),sQuery(id+"F0.wireOp",EDGE,"E160"),sQuery(id+"F0.wireOp",EDGE,"E163"),sQuery(id+"F0.wireOp",EDGE,"E161"),sQuery(id+"F0.wireOp",EDGE,"E162"),sQuery(id+"F0.wireOp",EDGE,"E151"),sQuery(id+"F0.wireOp",EDGE,"E152"),sQuery(id+"F0.wireOp",EDGE,"E153"),sQuery(id+"F0.wireOp",EDGE,"E167"),sQuery(id+"F0.wireOp",EDGE,"E168"),sQuery(id+"F0.wireOp",EDGE,"E169"),sQuery(id+"F0.wireOp",EDGE,"E166"),sQuery(id+"F0.wireOp",EDGE,"E165"),sQuery(id+"F0.wireOp",EDGE,"E164"),sQuery(id+"F0.wireOp",EDGE,"E170"),sQuery(id+"F0.wireOp",EDGE,"E171"),sQuery(id+"F0.wireOp",EDGE,"E172"),sQuery(id+"F0.wireOp",EDGE,"E173"),sQuery(id+"F0.wireOp",EDGE,"E174"),sQuery(id+"F0.wireOp",EDGE,"E175"),sQuery(id+"F0.wireOp",EDGE,"E176"),sQuery(id+"F0.wireOp",EDGE,"E177"),sQuery(id+"F0.wireOp",EDGE,"E178"),sQuery(id+"F0.wireOp",EDGE,"E138"),sQuery(id+"F0.wireOp",EDGE,"E179"),sQuery(id+"F0.wireOp",EDGE,"E180"),sQuery(id+"F0.wireOp",EDGE,"E181"),sQuery(id+"F0.wireOp",EDGE,"E182"),sQuery(id+"F0.wireOp",EDGE,"E183"),sQuery(id+"F0.wireOp",EDGE,"E184"),sQuery(id+"F0.wireOp",EDGE,"E185"),sQuery(id+"F0.wireOp",EDGE,"E186"),sQuery(id+"F0.wireOp",EDGE,"E187"),sQuery(id+"F0.wireOp",EDGE,"E188"),sQuery(id+"F0.wireOp",EDGE,"E191"),sQuery(id+"F0.wireOp",EDGE,"E192"),sQuery(id+"F0.wireOp",EDGE,"E189"),sQuery(id+"F0.wireOp",EDGE,"E190"),sQuery(id+"F0.wireOp",EDGE,"E193"),sQuery(id+"F0.wireOp",EDGE,"E194"),sQuery(id+"F0.wireOp",EDGE,"E195"),sQuery(id+"F0.wireOp",EDGE,"E196"),sQuery(id+"F0.wireOp",EDGE,"E197"),sQuery(id+"F0.wireOp",EDGE,"E198"),sQuery(id+"F0.wireOp",EDGE,"E199"),sQuery(id+"F0.wireOp",EDGE,"E200"),sQuery(id+"F0.wireOp",EDGE,"E201"),sQuery(id+"F0.wireOp",EDGE,"E203"),sQuery(id+"F0.wireOp",EDGE,"E204"),sQuery(id+"F0.wireOp",EDGE,"E205"),sQuery(id+"F0.wireOp",EDGE,"E206"),sQuery(id+"F0.wireOp",EDGE,"E207"),sQuery(id+"F0.wireOp",EDGE,"E208"),sQuery(id+"F0.wireOp",EDGE,"E209"),sQuery(id+"F0.wireOp",EDGE,"E202"),sQuery(id+"F0.wireOp",EDGE,"E210"),sQuery(id+"F0.wireOp",EDGE,"E211"),sQuery(id+"F0.wireOp",EDGE,"E212"),sQuery(id+"F0.wireOp",EDGE,"E213"),sQuery(id+"F0.wireOp",EDGE,"E214"),sQuery(id+"F0.wireOp",EDGE,"E215"),sQuery(id+"F0.wireOp",EDGE,"E216"),sQuery(id+"F0.wireOp",EDGE,"E217"),sQuery(id+"F0.wireOp",EDGE,"E218"),sQuery(id+"F0.wireOp",EDGE,"E219"),sQuery(id+"F0.wireOp",EDGE,"E234"),sQuery(id+"F0.wireOp",EDGE,"E236"),sQuery(id+"F0.wireOp",EDGE,"E235"),sQuery(id+"F0.wireOp",EDGE,"E220"),sQuery(id+"F0.wireOp",EDGE,"E221"),sQuery(id+"F0.wireOp",EDGE,"E222"),sQuery(id+"F0.wireOp",EDGE,"E223"),sQuery(id+"F0.wireOp",EDGE,"E224"),sQuery(id+"F0.wireOp",EDGE,"E225"),sQuery(id+"F0.wireOp",EDGE,"E226"),sQuery(id+"F0.wireOp",EDGE,"E227"),sQuery(id+"F0.wireOp",EDGE,"E228"),sQuery(id+"F0.wireOp",EDGE,"E229"),sQuery(id+"F0.wireOp",EDGE,"E230"),sQuery(id+"F0.wireOp",EDGE,"E231"),sQuery(id+"F0.wireOp",EDGE,"E233"),sQuery(id+"F0.wireOp",EDGE,"E232")])]});
            var Q1;
            Q1=makeQuery(id+"F3.boolean.opBoolean","COPY",FACE,{"derivedFrom":makeQuery(id+"F3.opExtrude","SWEPT_FACE",FACE,{"disambiguationData":[OSD([sQuery(id+"F2.wireOp",EDGE,"E239")])]})});
            mirror(context, id + "F4", {"operationType" : NewBodyOperationType.ADD, "entities" : qUnion([Q0]), "mirrorPlane" : qUnion([Q1])});
        }
        {
            var Q0;
            {var subQ0=makeQuery(id+"F1.opExtrude","SWEPT_FACE",FACE,{"disambiguationData":[OSD([sQuery(id+"F0.wireOp",EDGE,"E10")])]});Q0=makeQuery(id+"F4.boolean.opBoolean","MERGE",FACE,{"derivedFrom":[subQ0,makeQuery(id+"F4.opPattern","COPY",FACE,{"derivedFrom":subQ0,"instanceName":"1"})]});}
            var sketch = newSketch(context, id + "F5", { "sketchPlane" : qUnion([Q0])});
            skLineSegment(sketch, "E240", {"start": v(0, -889) * mm, "end": v(0, 911) * mm});
            skLineSegment(sketch, "E241", {"start": v(0, 911) * mm, "end": v(1800, 911) * mm});
            skLineSegment(sketch, "E242", {"start": v(1800, 911) * mm, "end": v(0, -889) * mm});
            skSolve(sketch);
        }
        {
            var Q0;
            {var subQ3=sQuery(id+"F5.wireOp",EDGE,"E241");Q0=makeQuery(id+"F5.imprint","IMPRINT",FACE,{"disambiguationData":[TD([[makeQuery(id+"F5.imprint","IMPRINT",EDGE,{"derivedFrom":subQ3}),-1.0]])]});}
            var Q1;
            {var subQ0=sQuery(id+"F5.wireOp",EDGE,"E242");var subQ1=sQuery(id+"F5.wireOp",EDGE,"E240");var subQ2=sQuery(id+"F0.wireOp",EDGE,"E10");var subQ3=makeQuery(id+"F5.imprint","INTERSECT",VERTEX,{"derivedFrom":[makeQuery(id+"F1.opExtrude","SWEPT_EDGE",EDGE,{"disambiguationData":[OSD([sQuery(id+"F0.wireOp",EDGE,"E0"),subQ2])]}),subQ1,subQ0]});Q1=makeQuery(id+"F5.imprint","IMPRINT",FACE,{"disambiguationData":[TD([[makeQuery(id+"F5.imprint","IMPRINT",EDGE,{"disambiguationData":[TD([[subQ3,1.0]])],"derivedFrom":subQ1}),1.0]])]});}
            extrude(context, id + "F6", {"entities" : qUnion([Q0, Q1]), "operationType" : NewBodyOperationType.REMOVE, "endBound" : BoundingType.THROUGH_ALL, "oppositeDirection" : true, "depth" : 25 * mm, "offsetDistance" : 25 * mm});
        }
        {
            var Q0;
            {var subQ0=makeQuery(id+"F1.opExtrude","SWEPT_FACE",FACE,{"disambiguationData":[OSD([sQuery(id+"F0.wireOp",EDGE,"E10")])]});Q0=makeQuery(id+"F4.boolean.opBoolean","MERGE",FACE,{"derivedFrom":[subQ0,makeQuery(id+"F4.opPattern","COPY",FACE,{"derivedFrom":subQ0,"instanceName":"1"})]});}
            var sketch = newSketch(context, id + "F7", { "sketchPlane" : qUnion([Q0])});
            skLineSegment(sketch, "E243", {"start": v(7000, 6111) * mm, "end": v(5200, 6111) * mm});
            skLineSegment(sketch, "E244", {"start": v(5200, 6111) * mm, "end": v(5200, 4311) * mm});
            skLineSegment(sketch, "E245", {"start": v(5200, 4311) * mm, "end": v(7000, 6111) * mm});
            skSolve(sketch);
        }
        {
            var Q0;
            {var subQ0=sQuery(id+"F7.wireOp",EDGE,"E245");var subQ1=sQuery(id+"F7.wireOp",EDGE,"E243");var subQ2=sQuery(id+"F0.wireOp",EDGE,"E10");var subQ3=makeQuery(id+"F7.imprint","INTERSECT",VERTEX,{"derivedFrom":[makeQuery(id+"F4.opPattern","COPY",EDGE,{"derivedFrom":makeQuery(id+"F1.opExtrude","SWEPT_EDGE",EDGE,{"disambiguationData":[OSD([sQuery(id+"F0.wireOp",EDGE,"E0"),subQ2])]}),"instanceName":"1"}),subQ1,subQ0]});Q0=makeQuery(id+"F7.imprint","IMPRINT",FACE,{"disambiguationData":[TD([[makeQuery(id+"F7.imprint","IMPRINT",EDGE,{"disambiguationData":[TD([[subQ3,1.0]])],"derivedFrom":subQ1}),-1.0]])]});}
            var Q1;
            {var subQ3=sQuery(id+"F7.wireOp",EDGE,"E244");Q1=makeQuery(id+"F7.imprint","IMPRINT",FACE,{"disambiguationData":[TD([[makeQuery(id+"F7.imprint","IMPRINT",EDGE,{"derivedFrom":subQ3}),1.0]])]});}
            extrude(context, id + "F8", {"entities" : qUnion([Q0, Q1]), "operationType" : NewBodyOperationType.REMOVE, "endBound" : BoundingType.THROUGH_ALL, "oppositeDirection" : true, "depth" : 25 * mm, "offsetDistance" : 25 * mm});
        }
    });
